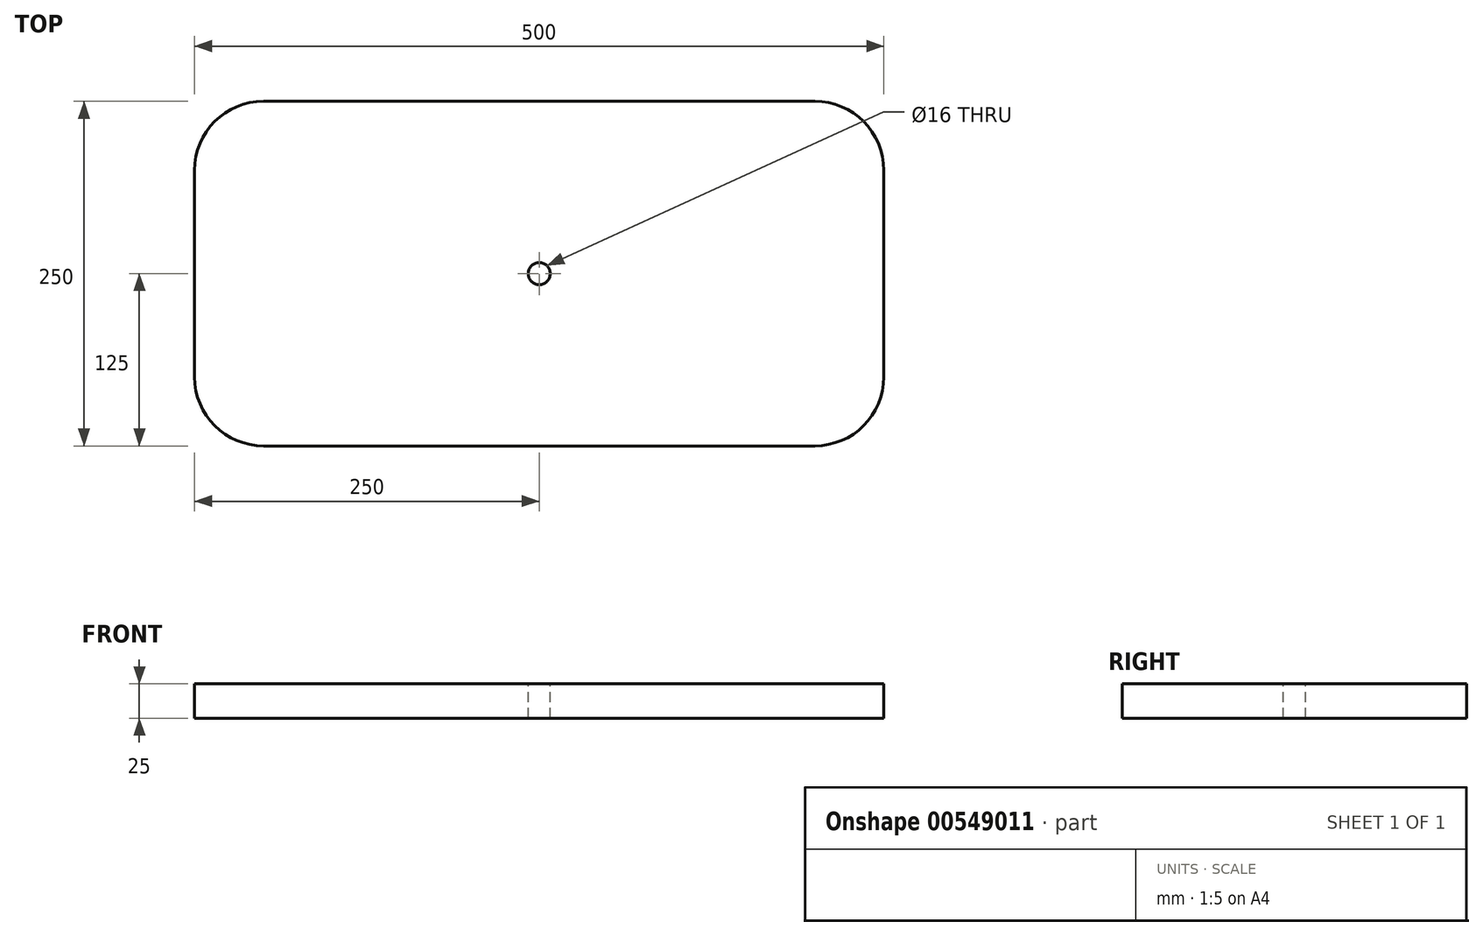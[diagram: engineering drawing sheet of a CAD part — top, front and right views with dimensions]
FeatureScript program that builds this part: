
annotation { "Feature Type Name" : "Feature", "Feature Type Description" : "" }
export const myFeature = defineFeature(function(context is Context, id is Id, definition is map)
    precondition{}
    {
        {
            var Q0;
            Q0=qCreatedBy(makeId("Top.planeOp"),FACE);
            var sketch = newSketch(context, id + "F0", { "sketchPlane" : qUnion([Q0])});
            skLineSegment(sketch, "E0.bottom", {"start": v(250, -125) * mm, "end": v(-250, -125) * mm});
            skLineSegment(sketch, "E0.top", {"start": v(250, 125) * mm, "end": v(-250, 125) * mm});
            skLineSegment(sketch, "E0.left", {"start": v(250, -125) * mm, "end": v(250, 125) * mm});
            skLineSegment(sketch, "E0.right", {"start": v(-250, -125) * mm, "end": v(-250, 125) * mm});
            skPoint(sketch, "E0.middle", {"position": v(0, 0) * mm});
            skSolve(sketch);
        }
        {
            var Q0;
            Q0=makeQuery(id+"F0.imprint","IMPRINT",FACE,{"disambiguationData":[TD([[makeQuery(id+"F0.imprint","IMPRINT",EDGE,{"derivedFrom":sQuery(id+"F0.wireOp",EDGE,"E0.bottom")}),-1.0]])]});
            extrude(context, id + "F1", {"entities" : qUnion([Q0]), "depth" : 25 * mm, "offsetDistance" : 25 * mm});
        }
        {
            var Q0;
            Q0=makeQuery(id+"F1.opExtrude","SWEPT_EDGE",EDGE,{"disambiguationData":[OSD([sQuery(id+"F0.wireOp",EDGE,"E0.bottom"),sQuery(id+"F0.wireOp",EDGE,"E0.right")])]});
            var Q1;
            Q1=makeQuery(id+"F1.opExtrude","SWEPT_EDGE",EDGE,{"disambiguationData":[OSD([sQuery(id+"F0.wireOp",EDGE,"E0.bottom"),sQuery(id+"F0.wireOp",EDGE,"E0.left")])]});
            var Q2;
            Q2=makeQuery(id+"F1.opExtrude","SWEPT_EDGE",EDGE,{"disambiguationData":[OSD([sQuery(id+"F0.wireOp",EDGE,"E0.top"),sQuery(id+"F0.wireOp",EDGE,"E0.left")])]});
            var Q3;
            Q3=makeQuery(id+"F1.opExtrude","SWEPT_EDGE",EDGE,{"disambiguationData":[OSD([sQuery(id+"F0.wireOp",EDGE,"E0.top"),sQuery(id+"F0.wireOp",EDGE,"E0.right")])]});
            fillet(context, id + "F2", {"entities" : qUnion([Q0, Q1, Q2, Q3]), "radius" : 50 * mm, "tangentPropagation" : true, "allowEdgeOverflow" : false});
        }
        {
            var Q0;
            Q0=makeQuery(id+"F1.opExtrude","CAP_FACE",FACE,{"disambiguationData":[OSD([sQuery(id+"F0.wireOp",EDGE,"E0.bottom"),sQuery(id+"F0.wireOp",EDGE,"E0.top"),sQuery(id+"F0.wireOp",EDGE,"E0.left"),sQuery(id+"F0.wireOp",EDGE,"E0.right")])],"isStart":false});
            var sketch = newSketch(context, id + "F3", { "sketchPlane" : qUnion([Q0])});
            skCircle(sketch, "E1", {"center": v(0, 0) * mm, "radius": 8 * mm});
            skSolve(sketch);
        }
        {
            var Q0;
            Q0=makeQuery(id+"F3.imprint","IMPRINT",FACE,{"disambiguationData":[TD([[makeQuery(id+"F3.imprint","IMPRINT",EDGE,{"derivedFrom":sQuery(id+"F3.wireOp",EDGE,"E1")}),1.0]])]});
            extrude(context, id + "F4", {"entities" : qUnion([Q0]), "operationType" : NewBodyOperationType.REMOVE, "endBound" : BoundingType.THROUGH_ALL, "oppositeDirection" : true, "depth" : 25 * mm, "offsetDistance" : 25 * mm});
        }
    });
